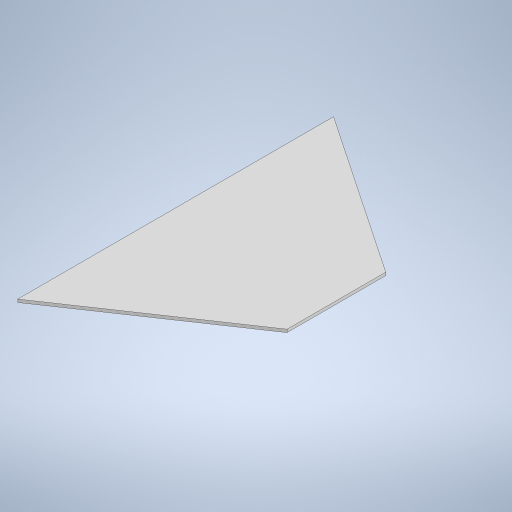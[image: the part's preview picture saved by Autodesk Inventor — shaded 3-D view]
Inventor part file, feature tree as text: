
AUTODESK INVENTOR PART (.ipt)
format: ipt  version: 2024.3 (Build 283343000, 343)  size: 218,112 bytes
history: native  units: mm
features: extrude x1, sketch x1
ambient origin geometry x8: Origin, YZ Plane, XZ Plane, XY Plane, X Axis, Y Axis, Z Axis, Center Point
bodies: Solid1 (feature_tree)
feature tree (2):
  extrude  "Extrusion1"  Depth=162.865mm
  sketch  "Sketch1"  dims[d0=320.0mm d1=162.865mm d2=100.0mm d3=50.0mm d4=3.0mm d5=0.0mm]
